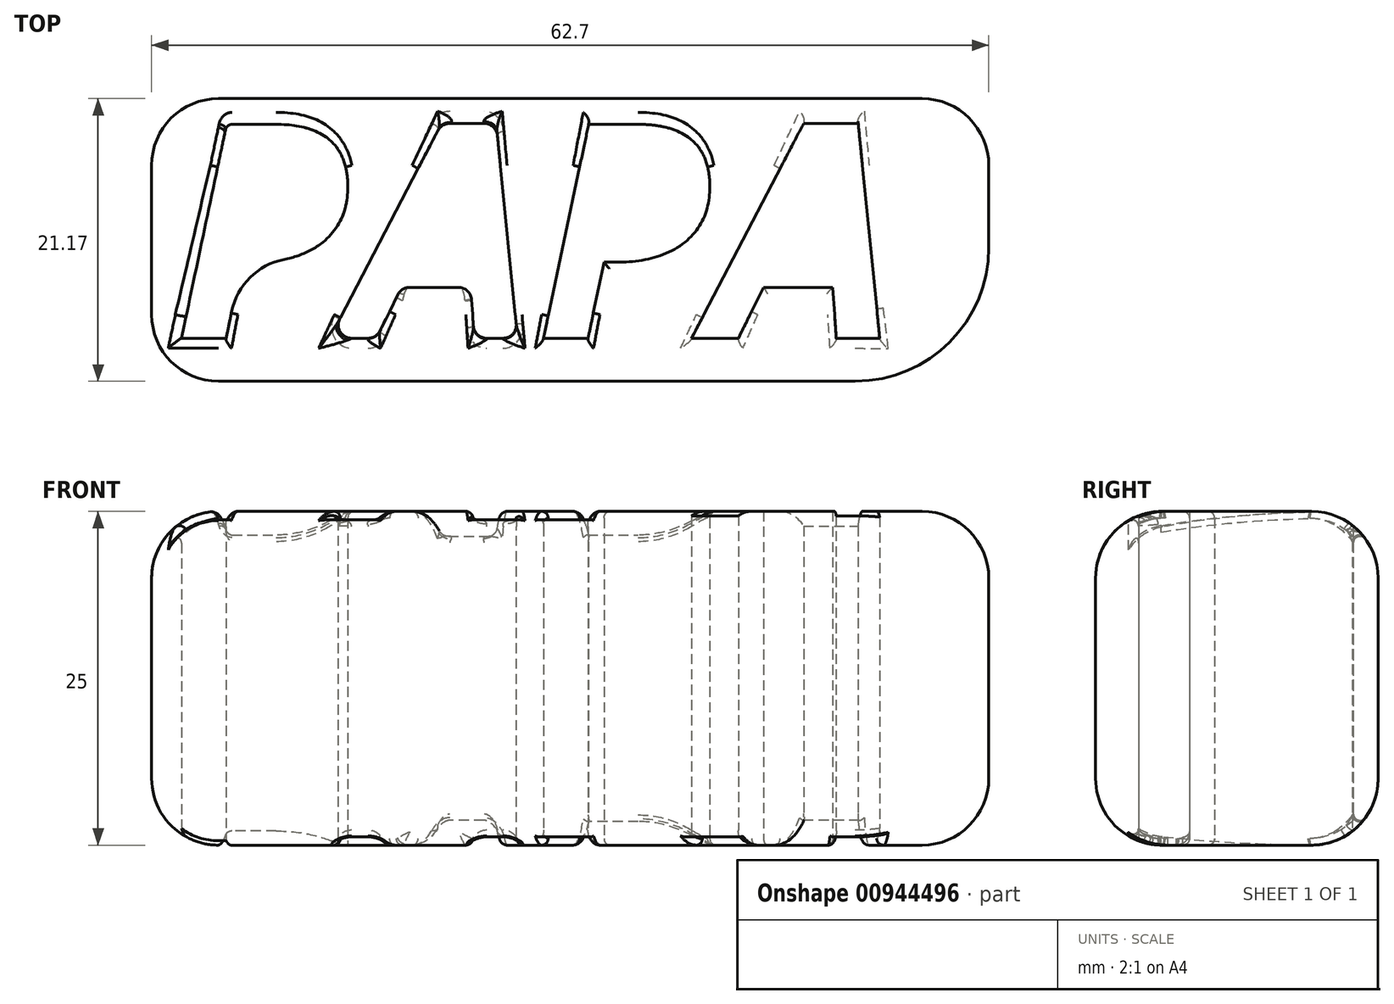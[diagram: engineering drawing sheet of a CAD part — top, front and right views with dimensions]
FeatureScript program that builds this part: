
annotation { "Feature Type Name" : "Feature", "Feature Type Description" : "" }
export const myFeature = defineFeature(function(context is Context, id is Id, definition is map)
    precondition{}
    {
        {
            var Q0;
            Q0=qCreatedBy(makeId("Top.planeOp"),FACE);
            var sketch = newSketch(context, id + "F0", { "sketchPlane" : qUnion([Q0])});
            skText(sketch, "E0", { "text": "PAPA", "fontName": "OpenSans-BoldItalic.ttf"});
            skLineSegment(sketch, "E1.bottom", {"start": v(-61.02, -20.6) * mm, "end": v(-8.32, -20.6) * mm});
            skLineSegment(sketch, "E1.top", {"start": v(-61.02, -41.77) * mm, "end": v(-13.32, -41.77) * mm});
            skLineSegment(sketch, "E1.left", {"start": v(-66.02, -25.6) * mm, "end": v(-66.02, -36.77) * mm});
            skLineSegment(sketch, "E1.right", {"start": v(-3.32, -25.6) * mm, "end": v(-3.32, -31.77) * mm});
            skPoint(sketch, "E2.visualSharp", {"position": v(-3.32, -20.6) * mm});
            skArc(sketch, "E2.filletArc", {"start": v(-3.32, -25.6) * mm, "mid": v(-4.78, -22.07) * mm, "end": v(-8.32, -20.6) * mm});
            skPoint(sketch, "E3.visualSharp", {"position": v(-66.02, -41.77) * mm});
            skArc(sketch, "E3.filletArc", {"start": v(-66.02, -36.77) * mm, "mid": v(-64.56, -40.3) * mm, "end": v(-61.02, -41.77) * mm});
            skPoint(sketch, "E4.visualSharp", {"position": v(-66.02, -20.6) * mm});
            skArc(sketch, "E4.filletArc", {"start": v(-61.02, -20.6) * mm, "mid": v(-64.56, -22.07) * mm, "end": v(-66.02, -25.6) * mm});
            skPoint(sketch, "E5.visualSharp", {"position": v(-3.32, -41.77) * mm});
            skArc(sketch, "E5.filletArc", {"start": v(-13.32, -41.77) * mm, "mid": v(-6.24, -38.84) * mm, "end": v(-3.32, -31.77) * mm});
            const initialGuessF0  = {"E0": [-0.06437, -0.03855, 1, 0, 0.01616]};
            skSetInitialGuess(sketch, initialGuessF0);
            skSolve(sketch);
        }
        {
            var Q0;
            Q0=makeQuery(id+"F0.imprint","IMPRINT",FACE,{"disambiguationData":[TD([[makeQuery(id+"F0.imprint","IMPRINT",EDGE,{"derivedFrom":sQuery(id+"F0.wireOp",EDGE,"E0.sketch_text.stroke-6")}),1.0]])]});
            extrude(context, id + "F1", {"entities" : qUnion([Q0]), "depth" : 25 * mm, "offsetDistance" : 25 * mm});
        }
        {
            var Q0;
            Q0=makeQuery(id+"F1.opExtrude","CAP_EDGE",EDGE,{"disambiguationData":[OSD([sQuery(id+"F0.wireOp",EDGE,"E1.bottom")])],"isStart":false});
            var Q1;
            Q1=makeQuery(id+"F1.opExtrude","CAP_EDGE",EDGE,{"disambiguationData":[OSD([sQuery(id+"F0.wireOp",EDGE,"E1.bottom")])],"isStart":true});
            fillet(context, id + "F2", {"entities" : qUnion([Q0, Q1]), "radius" : 5 * mm, "tangentPropagation" : true, "allowEdgeOverflow" : false});
        }
        {
            var Q0;
            Q0=makeQuery(id+"F2.opFillet","BLEND_EDGE",EDGE,{"blendedFrom":[makeQuery(id+"F1.opExtrude","CAP_EDGE",EDGE,{"disambiguationData":[OSD([sQuery(id+"F0.wireOp",EDGE,"E1.bottom")])],"isStart":false}),makeQuery(id+"F1.opExtrude","SWEPT_FACE",FACE,{"disambiguationData":[OSD([sQuery(id+"F0.wireOp",EDGE,"E0.sketch_text.stroke-12")])]})],"blendedInto":[makeQuery(id+"F1.opExtrude","SWEPT_FACE",FACE,{"disambiguationData":[OSD([sQuery(id+"F0.wireOp",EDGE,"E0.sketch_text.stroke-12")])]})]});
            var Q1;
            Q1=makeQuery(id+"F2.opFillet","BLEND_EDGE",EDGE,{"blendedFrom":[makeQuery(id+"F1.opExtrude","CAP_EDGE",EDGE,{"disambiguationData":[OSD([sQuery(id+"F0.wireOp",EDGE,"E1.bottom")])],"isStart":false}),makeQuery(id+"F1.opExtrude","SWEPT_FACE",FACE,{"disambiguationData":[OSD([sQuery(id+"F0.wireOp",EDGE,"E0.sketch_text.stroke-13")])]})],"blendedInto":[makeQuery(id+"F1.opExtrude","SWEPT_FACE",FACE,{"disambiguationData":[OSD([sQuery(id+"F0.wireOp",EDGE,"E0.sketch_text.stroke-13")])]})]});
            var Q2;
            Q2=makeQuery(id+"F1.opExtrude","CAP_EDGE",EDGE,{"disambiguationData":[OSD([sQuery(id+"F0.wireOp",EDGE,"E0.sketch_text.stroke-14")])],"isStart":false});
            var Q3;
            Q3=makeQuery(id+"F1.opExtrude","CAP_EDGE",EDGE,{"disambiguationData":[OSD([sQuery(id+"F0.wireOp",EDGE,"E0.sketch_text.stroke-6")])],"isStart":false});
            var Q4;
            Q4=makeQuery(id+"F1.opExtrude","CAP_EDGE",EDGE,{"disambiguationData":[OSD([sQuery(id+"F0.wireOp",EDGE,"E0.sketch_text.stroke-7")])],"isStart":false});
            var Q5;
            Q5=makeQuery(id+"F2.opFillet","BLEND_EDGE",EDGE,{"blendedFrom":[makeQuery(id+"F1.opExtrude","CAP_EDGE",EDGE,{"disambiguationData":[OSD([sQuery(id+"F0.wireOp",EDGE,"E1.bottom")])],"isStart":false}),makeQuery(id+"F1.opExtrude","SWEPT_FACE",FACE,{"disambiguationData":[OSD([sQuery(id+"F0.wireOp",EDGE,"E0.sketch_text.stroke-14")])]})],"blendedInto":[makeQuery(id+"F1.opExtrude","SWEPT_FACE",FACE,{"disambiguationData":[OSD([sQuery(id+"F0.wireOp",EDGE,"E0.sketch_text.stroke-14")])]})]});
            var Q6;
            Q6=makeQuery(id+"F1.opExtrude","CAP_EDGE",EDGE,{"disambiguationData":[OSD([sQuery(id+"F0.wireOp",EDGE,"E0.sketch_text.stroke-8")])],"isStart":false});
            var Q7;
            Q7=makeQuery(id+"F1.opExtrude","CAP_EDGE",EDGE,{"disambiguationData":[OSD([sQuery(id+"F0.wireOp",EDGE,"E0.sketch_text.stroke-9")])],"isStart":false});
            var Q8;
            Q8=makeQuery(id+"F2.opFillet","BLEND_EDGE",EDGE,{"blendedFrom":[makeQuery(id+"F1.opExtrude","CAP_EDGE",EDGE,{"disambiguationData":[OSD([sQuery(id+"F0.wireOp",EDGE,"E1.top")])],"isStart":false}),makeQuery(id+"F1.opExtrude","SWEPT_FACE",FACE,{"disambiguationData":[OSD([sQuery(id+"F0.wireOp",EDGE,"E0.sketch_text.stroke-9")])]})],"blendedInto":[makeQuery(id+"F1.opExtrude","SWEPT_FACE",FACE,{"disambiguationData":[OSD([sQuery(id+"F0.wireOp",EDGE,"E0.sketch_text.stroke-9")])]})]});
            var Q9;
            Q9=makeQuery(id+"F2.opFillet","BLEND_EDGE",EDGE,{"disambiguationData":[OD(0.0)],"blendedFrom":[makeQuery(id+"F1.opExtrude","CAP_EDGE",EDGE,{"disambiguationData":[OSD([sQuery(id+"F0.wireOp",EDGE,"E1.top")])],"isStart":false}),makeQuery(id+"F1.opExtrude","SWEPT_FACE",FACE,{"disambiguationData":[OSD([sQuery(id+"F0.wireOp",EDGE,"E0.sketch_text.stroke-10")])]})],"blendedInto":[makeQuery(id+"F1.opExtrude","SWEPT_FACE",FACE,{"disambiguationData":[OSD([sQuery(id+"F0.wireOp",EDGE,"E0.sketch_text.stroke-10")])]})]});
            var Q10;
            Q10=makeQuery(id+"F2.opFillet","BLEND_EDGE",EDGE,{"disambiguationData":[OD(2.0)],"blendedFrom":[makeQuery(id+"F1.opExtrude","CAP_EDGE",EDGE,{"disambiguationData":[OSD([sQuery(id+"F0.wireOp",EDGE,"E1.top")])],"isStart":false}),makeQuery(id+"F1.opExtrude","SWEPT_FACE",FACE,{"disambiguationData":[OSD([sQuery(id+"F0.wireOp",EDGE,"E0.sketch_text.stroke-11")])]})],"blendedInto":[makeQuery(id+"F1.opExtrude","SWEPT_FACE",FACE,{"disambiguationData":[OSD([sQuery(id+"F0.wireOp",EDGE,"E0.sketch_text.stroke-11")])]})]});
            var Q11;
            Q11=makeQuery(id+"F2.opFillet","BLEND_EDGE",EDGE,{"disambiguationData":[OD(1.0)],"blendedFrom":[makeQuery(id+"F1.opExtrude","CAP_EDGE",EDGE,{"disambiguationData":[OSD([sQuery(id+"F0.wireOp",EDGE,"E1.top")])],"isStart":false}),makeQuery(id+"F1.opExtrude","SWEPT_FACE",FACE,{"disambiguationData":[OSD([sQuery(id+"F0.wireOp",EDGE,"E0.sketch_text.stroke-11")])]})],"blendedInto":[makeQuery(id+"F1.opExtrude","SWEPT_FACE",FACE,{"disambiguationData":[OSD([sQuery(id+"F0.wireOp",EDGE,"E0.sketch_text.stroke-11")])]})]});
            var Q12;
            Q12=makeQuery(id+"F2.opFillet","BLEND_EDGE",EDGE,{"blendedFrom":[makeQuery(id+"F1.opExtrude","CAP_EDGE",EDGE,{"disambiguationData":[OSD([sQuery(id+"F0.wireOp",EDGE,"E1.bottom")])],"isStart":false}),makeQuery(id+"F1.opExtrude","SWEPT_FACE",FACE,{"disambiguationData":[OSD([sQuery(id+"F0.wireOp",EDGE,"E0.sketch_text.stroke-11")])]})],"blendedInto":[makeQuery(id+"F1.opExtrude","SWEPT_FACE",FACE,{"disambiguationData":[OSD([sQuery(id+"F0.wireOp",EDGE,"E0.sketch_text.stroke-11")])]})]});
            var Q13;
            Q13=makeQuery(id+"F1.opExtrude","SWEPT_EDGE",EDGE,{"disambiguationData":[OSD([sQuery(id+"F0.wireOp",EDGE,"E0.sketch_text.stroke-11"),sQuery(id+"F0.wireOp",EDGE,"E0.sketch_text.stroke-12")])]});
            var Q14;
            Q14=makeQuery(id+"F2.opFillet","BLEND_EDGE",EDGE,{"disambiguationData":[OD(1.0)],"blendedFrom":[makeQuery(id+"F1.opExtrude","CAP_EDGE",EDGE,{"disambiguationData":[OSD([sQuery(id+"F0.wireOp",EDGE,"E1.top")])],"isStart":false}),makeQuery(id+"F1.opExtrude","SWEPT_FACE",FACE,{"disambiguationData":[OSD([sQuery(id+"F0.wireOp",EDGE,"E0.sketch_text.stroke-10")])]})],"blendedInto":[makeQuery(id+"F1.opExtrude","SWEPT_FACE",FACE,{"disambiguationData":[OSD([sQuery(id+"F0.wireOp",EDGE,"E0.sketch_text.stroke-10")])]})]});
            fillet(context, id + "F3", {"entities" : qUnion([Q0, Q1, Q2, Q3, Q4, Q5, Q6, Q7, Q8, Q9, Q10, Q11, Q12, Q13, Q14]), "radius" : 0.5 * mm, "tangentPropagation" : true, "allowEdgeOverflow" : false});
        }
        {
            var Q0;
            Q0=makeQuery(id+"F2.opFillet","BLEND_EDGE",EDGE,{"blendedFrom":[makeQuery(id+"F1.opExtrude","CAP_EDGE",EDGE,{"disambiguationData":[OSD([sQuery(id+"F0.wireOp",EDGE,"E1.bottom")])],"isStart":false}),makeQuery(id+"F1.opExtrude","SWEPT_FACE",FACE,{"disambiguationData":[OSD([sQuery(id+"F0.wireOp",EDGE,"E0.sketch_text.stroke-20")])]})],"blendedInto":[makeQuery(id+"F1.opExtrude","SWEPT_FACE",FACE,{"disambiguationData":[OSD([sQuery(id+"F0.wireOp",EDGE,"E0.sketch_text.stroke-20")])]})]});
            var Q1;
            Q1=makeQuery(id+"F2.opFillet","BLEND_EDGE",EDGE,{"blendedFrom":[makeQuery(id+"F1.opExtrude","CAP_EDGE",EDGE,{"disambiguationData":[OSD([sQuery(id+"F0.wireOp",EDGE,"E1.bottom")])],"isStart":false}),makeQuery(id+"F1.opExtrude","SWEPT_FACE",FACE,{"disambiguationData":[OSD([sQuery(id+"F0.wireOp",EDGE,"E0.sketch_text.stroke-18")])]})],"blendedInto":[makeQuery(id+"F1.opExtrude","SWEPT_FACE",FACE,{"disambiguationData":[OSD([sQuery(id+"F0.wireOp",EDGE,"E0.sketch_text.stroke-18")])]})]});
            var Q2;
            Q2=makeQuery(id+"F1.opExtrude","CAP_EDGE",EDGE,{"disambiguationData":[OSD([sQuery(id+"F0.wireOp",EDGE,"E0.sketch_text.stroke-18")])],"isStart":false});
            var Q3;
            Q3=makeQuery(id+"F1.opExtrude","CAP_EDGE",EDGE,{"disambiguationData":[OSD([sQuery(id+"F0.wireOp",EDGE,"E0.sketch_text.stroke-20")])],"isStart":false});
            var Q4;
            Q4=makeQuery(id+"F2.opFillet","BLEND_EDGE",EDGE,{"blendedFrom":[makeQuery(id+"F1.opExtrude","CAP_EDGE",EDGE,{"disambiguationData":[OSD([sQuery(id+"F0.wireOp",EDGE,"E1.top")])],"isStart":false}),makeQuery(id+"F1.opExtrude","SWEPT_FACE",FACE,{"disambiguationData":[OSD([sQuery(id+"F0.wireOp",EDGE,"E0.sketch_text.stroke-20")])]})],"blendedInto":[makeQuery(id+"F1.opExtrude","SWEPT_FACE",FACE,{"disambiguationData":[OSD([sQuery(id+"F0.wireOp",EDGE,"E0.sketch_text.stroke-20")])]})]});
            var Q5;
            Q5=makeQuery(id+"F2.opFillet","BLEND_EDGE",EDGE,{"blendedFrom":[makeQuery(id+"F1.opExtrude","CAP_EDGE",EDGE,{"disambiguationData":[OSD([sQuery(id+"F0.wireOp",EDGE,"E1.top")])],"isStart":false}),makeQuery(id+"F1.opExtrude","SWEPT_FACE",FACE,{"disambiguationData":[OSD([sQuery(id+"F0.wireOp",EDGE,"E0.sketch_text.stroke-21")])]})],"blendedInto":[makeQuery(id+"F1.opExtrude","SWEPT_FACE",FACE,{"disambiguationData":[OSD([sQuery(id+"F0.wireOp",EDGE,"E0.sketch_text.stroke-21")])]})]});
            var Q6;
            Q6=makeQuery(id+"F2.opFillet","BLEND_EDGE",EDGE,{"blendedFrom":[makeQuery(id+"F1.opExtrude","CAP_EDGE",EDGE,{"disambiguationData":[OSD([sQuery(id+"F0.wireOp",EDGE,"E1.top")])],"isStart":false}),makeQuery(id+"F1.opExtrude","SWEPT_FACE",FACE,{"disambiguationData":[OSD([sQuery(id+"F0.wireOp",EDGE,"E0.sketch_text.stroke-22")])]})],"blendedInto":[makeQuery(id+"F1.opExtrude","SWEPT_FACE",FACE,{"disambiguationData":[OSD([sQuery(id+"F0.wireOp",EDGE,"E0.sketch_text.stroke-22")])]})]});
            var Q7;
            Q7=makeQuery(id+"F1.opExtrude","CAP_EDGE",EDGE,{"disambiguationData":[OSD([sQuery(id+"F0.wireOp",EDGE,"E0.sketch_text.stroke-22")])],"isStart":false});
            var Q8;
            Q8=makeQuery(id+"F1.opExtrude","CAP_EDGE",EDGE,{"disambiguationData":[OSD([sQuery(id+"F0.wireOp",EDGE,"E0.sketch_text.stroke-15")])],"isStart":false});
            var Q9;
            Q9=makeQuery(id+"F1.opExtrude","CAP_EDGE",EDGE,{"disambiguationData":[OSD([sQuery(id+"F0.wireOp",EDGE,"E0.sketch_text.stroke-16")])],"isStart":false});
            var Q10;
            Q10=makeQuery(id+"F2.opFillet","BLEND_EDGE",EDGE,{"blendedFrom":[makeQuery(id+"F1.opExtrude","CAP_EDGE",EDGE,{"disambiguationData":[OSD([sQuery(id+"F0.wireOp",EDGE,"E1.top")])],"isStart":false}),makeQuery(id+"F1.opExtrude","SWEPT_FACE",FACE,{"disambiguationData":[OSD([sQuery(id+"F0.wireOp",EDGE,"E0.sketch_text.stroke-16")])]})],"blendedInto":[makeQuery(id+"F1.opExtrude","SWEPT_FACE",FACE,{"disambiguationData":[OSD([sQuery(id+"F0.wireOp",EDGE,"E0.sketch_text.stroke-16")])]})]});
            var Q11;
            Q11=makeQuery(id+"F2.opFillet","BLEND_EDGE",EDGE,{"blendedFrom":[makeQuery(id+"F1.opExtrude","CAP_EDGE",EDGE,{"disambiguationData":[OSD([sQuery(id+"F0.wireOp",EDGE,"E1.top")])],"isStart":false}),makeQuery(id+"F1.opExtrude","SWEPT_FACE",FACE,{"disambiguationData":[OSD([sQuery(id+"F0.wireOp",EDGE,"E0.sketch_text.stroke-17")])]})],"blendedInto":[makeQuery(id+"F1.opExtrude","SWEPT_FACE",FACE,{"disambiguationData":[OSD([sQuery(id+"F0.wireOp",EDGE,"E0.sketch_text.stroke-17")])]})]});
            var Q12;
            Q12=makeQuery(id+"F2.opFillet","BLEND_EDGE",EDGE,{"blendedFrom":[makeQuery(id+"F1.opExtrude","CAP_EDGE",EDGE,{"disambiguationData":[OSD([sQuery(id+"F0.wireOp",EDGE,"E1.top")])],"isStart":false}),makeQuery(id+"F1.opExtrude","SWEPT_FACE",FACE,{"disambiguationData":[OSD([sQuery(id+"F0.wireOp",EDGE,"E0.sketch_text.stroke-18")])]})],"blendedInto":[makeQuery(id+"F1.opExtrude","SWEPT_FACE",FACE,{"disambiguationData":[OSD([sQuery(id+"F0.wireOp",EDGE,"E0.sketch_text.stroke-18")])]})]});
            var Q13;
            Q13=makeQuery(id+"F2.opFillet","BLEND_EDGE",EDGE,{"blendedFrom":[makeQuery(id+"F1.opExtrude","CAP_EDGE",EDGE,{"disambiguationData":[OSD([sQuery(id+"F0.wireOp",EDGE,"E1.bottom")])],"isStart":false}),makeQuery(id+"F1.opExtrude","SWEPT_FACE",FACE,{"disambiguationData":[OSD([sQuery(id+"F0.wireOp",EDGE,"E0.sketch_text.stroke-19")])]})],"blendedInto":[makeQuery(id+"F1.opExtrude","SWEPT_FACE",FACE,{"disambiguationData":[OSD([sQuery(id+"F0.wireOp",EDGE,"E0.sketch_text.stroke-19")])]})]});
            fillet(context, id + "F4", {"entities" : qUnion([Q0, Q1, Q2, Q3, Q4, Q5, Q6, Q7, Q8, Q9, Q10, Q11, Q12, Q13]), "radius" : 0.5 * mm, "tangentPropagation" : true, "allowEdgeOverflow" : false});
        }
        {
            var Q0;
            Q0=makeQuery(id+"F1.opExtrude","SWEPT_EDGE",EDGE,{"disambiguationData":[OSD([sQuery(id+"F0.wireOp",EDGE,"E0.sketch_text.stroke-8"),sQuery(id+"F0.wireOp",EDGE,"E0.sketch_text.stroke-9")])]});
            fillet(context, id + "F5", {"entities" : qUnion([Q0]), "radius" : 5 * mm, "tangentPropagation" : true, "allowEdgeOverflow" : false});
        }
        {
            var Q0;
            Q0=makeQuery(id+"F1.opExtrude","SWEPT_EDGE",EDGE,{"disambiguationData":[OSD([sQuery(id+"F0.wireOp",EDGE,"E0.sketch_text.stroke-15"),sQuery(id+"F0.wireOp",EDGE,"E0.sketch_text.stroke-16")])]});
            var Q1;
            Q1=makeQuery(id+"F1.opExtrude","SWEPT_FACE",FACE,{"disambiguationData":[OSD([sQuery(id+"F0.wireOp",EDGE,"E0.sketch_text.stroke-15")])]});
            var Q2;
            Q2=makeQuery(id+"F1.opExtrude","SWEPT_EDGE",EDGE,{"disambiguationData":[OSD([sQuery(id+"F0.wireOp",EDGE,"E0.sketch_text.stroke-20"),sQuery(id+"F0.wireOp",EDGE,"E0.sketch_text.stroke-21")])]});
            var Q3;
            Q3=makeQuery(id+"F1.opExtrude","SWEPT_EDGE",EDGE,{"disambiguationData":[OSD([sQuery(id+"F0.wireOp",EDGE,"E0.sketch_text.stroke-21"),sQuery(id+"F0.wireOp",EDGE,"E0.sketch_text.stroke-22")])]});
            var Q4;
            Q4=makeQuery(id+"F1.opExtrude","SWEPT_EDGE",EDGE,{"disambiguationData":[OSD([sQuery(id+"F0.wireOp",EDGE,"E0.sketch_text.stroke-16"),sQuery(id+"F0.wireOp",EDGE,"E0.sketch_text.stroke-17")])]});
            var Q5;
            Q5=makeQuery(id+"F1.opExtrude","SWEPT_EDGE",EDGE,{"disambiguationData":[OSD([sQuery(id+"F0.wireOp",EDGE,"E0.sketch_text.stroke-17"),sQuery(id+"F0.wireOp",EDGE,"E0.sketch_text.stroke-18")])]});
            var Q6;
            Q6=makeQuery(id+"F1.opExtrude","SWEPT_EDGE",EDGE,{"disambiguationData":[OSD([sQuery(id+"F0.wireOp",EDGE,"E0.sketch_text.stroke-19"),sQuery(id+"F0.wireOp",EDGE,"E0.sketch_text.stroke-20")])]});
            var Q7;
            Q7=makeQuery(id+"F1.opExtrude","SWEPT_EDGE",EDGE,{"disambiguationData":[OSD([sQuery(id+"F0.wireOp",EDGE,"E0.sketch_text.stroke-18"),sQuery(id+"F0.wireOp",EDGE,"E0.sketch_text.stroke-19")])]});
            fillet(context, id + "F6", {"entities" : qUnion([Q0, Q1, Q2, Q3, Q4, Q5, Q6, Q7]), "radius" : 1 * mm, "tangentPropagation" : true, "allowEdgeOverflow" : false});
        }
        {
            var Q0;
            Q0=makeQuery(id+"F2.opFillet","BLEND_EDGE",EDGE,{"blendedFrom":[makeQuery(id+"F1.opExtrude","CAP_EDGE",EDGE,{"disambiguationData":[OSD([sQuery(id+"F0.wireOp",EDGE,"E1.bottom")])],"isStart":false}),makeQuery(id+"F1.opExtrude","SWEPT_FACE",FACE,{"disambiguationData":[OSD([sQuery(id+"F0.wireOp",EDGE,"E0.sketch_text.stroke-41")])]})],"blendedInto":[makeQuery(id+"F1.opExtrude","SWEPT_FACE",FACE,{"disambiguationData":[OSD([sQuery(id+"F0.wireOp",EDGE,"E0.sketch_text.stroke-41")])]})]});
            var Q1;
            Q1=makeQuery(id+"F2.opFillet","BLEND_EDGE",EDGE,{"blendedFrom":[makeQuery(id+"F1.opExtrude","CAP_EDGE",EDGE,{"disambiguationData":[OSD([sQuery(id+"F0.wireOp",EDGE,"E1.bottom")])],"isStart":false}),makeQuery(id+"F1.opExtrude","SWEPT_FACE",FACE,{"disambiguationData":[OSD([sQuery(id+"F0.wireOp",EDGE,"E0.sketch_text.stroke-42")])]})],"blendedInto":[makeQuery(id+"F1.opExtrude","SWEPT_FACE",FACE,{"disambiguationData":[OSD([sQuery(id+"F0.wireOp",EDGE,"E0.sketch_text.stroke-42")])]})]});
            var Q2;
            Q2=makeQuery(id+"F2.opFillet","BLEND_EDGE",EDGE,{"blendedFrom":[makeQuery(id+"F1.opExtrude","CAP_EDGE",EDGE,{"disambiguationData":[OSD([sQuery(id+"F0.wireOp",EDGE,"E1.bottom")])],"isStart":false}),makeQuery(id+"F1.opExtrude","SWEPT_FACE",FACE,{"disambiguationData":[OSD([sQuery(id+"F0.wireOp",EDGE,"E0.sketch_text.stroke-43")])]})],"blendedInto":[makeQuery(id+"F1.opExtrude","SWEPT_FACE",FACE,{"disambiguationData":[OSD([sQuery(id+"F0.wireOp",EDGE,"E0.sketch_text.stroke-43")])]})]});
            var Q3;
            Q3=makeQuery(id+"F1.opExtrude","CAP_EDGE",EDGE,{"disambiguationData":[OSD([sQuery(id+"F0.wireOp",EDGE,"E0.sketch_text.stroke-43")])],"isStart":false});
            var Q4;
            Q4=makeQuery(id+"F1.opExtrude","CAP_EDGE",EDGE,{"disambiguationData":[OSD([sQuery(id+"F0.wireOp",EDGE,"E0.sketch_text.stroke-35")])],"isStart":false});
            var Q5;
            Q5=makeQuery(id+"F1.opExtrude","CAP_EDGE",EDGE,{"disambiguationData":[OSD([sQuery(id+"F0.wireOp",EDGE,"E0.sketch_text.stroke-36")])],"isStart":false});
            var Q6;
            Q6=makeQuery(id+"F1.opExtrude","CAP_EDGE",EDGE,{"disambiguationData":[OSD([sQuery(id+"F0.wireOp",EDGE,"E0.sketch_text.stroke-38")])],"isStart":false});
            var Q7;
            Q7=makeQuery(id+"F2.opFillet","BLEND_EDGE",EDGE,{"blendedFrom":[makeQuery(id+"F1.opExtrude","CAP_EDGE",EDGE,{"disambiguationData":[OSD([sQuery(id+"F0.wireOp",EDGE,"E1.top")])],"isStart":false}),makeQuery(id+"F1.opExtrude","SWEPT_FACE",FACE,{"disambiguationData":[OSD([sQuery(id+"F0.wireOp",EDGE,"E0.sketch_text.stroke-38")])]})],"blendedInto":[makeQuery(id+"F1.opExtrude","SWEPT_FACE",FACE,{"disambiguationData":[OSD([sQuery(id+"F0.wireOp",EDGE,"E0.sketch_text.stroke-38")])]})]});
            var Q8;
            Q8=makeQuery(id+"F2.opFillet","BLEND_EDGE",EDGE,{"blendedFrom":[makeQuery(id+"F1.opExtrude","CAP_EDGE",EDGE,{"disambiguationData":[OSD([sQuery(id+"F0.wireOp",EDGE,"E1.top")])],"isStart":false}),makeQuery(id+"F1.opExtrude","SWEPT_FACE",FACE,{"disambiguationData":[OSD([sQuery(id+"F0.wireOp",EDGE,"E0.sketch_text.stroke-39")])]})],"blendedInto":[makeQuery(id+"F1.opExtrude","SWEPT_FACE",FACE,{"disambiguationData":[OSD([sQuery(id+"F0.wireOp",EDGE,"E0.sketch_text.stroke-39")])]})]});
            var Q9;
            Q9=makeQuery(id+"F2.opFillet","BLEND_EDGE",EDGE,{"blendedFrom":[makeQuery(id+"F1.opExtrude","CAP_EDGE",EDGE,{"disambiguationData":[OSD([sQuery(id+"F0.wireOp",EDGE,"E1.top")])],"isStart":false}),makeQuery(id+"F1.opExtrude","SWEPT_FACE",FACE,{"disambiguationData":[OSD([sQuery(id+"F0.wireOp",EDGE,"E0.sketch_text.stroke-40")])]})],"blendedInto":[makeQuery(id+"F1.opExtrude","SWEPT_FACE",FACE,{"disambiguationData":[OSD([sQuery(id+"F0.wireOp",EDGE,"E0.sketch_text.stroke-40")])]})]});
            var Q10;
            Q10=makeQuery(id+"F1.opExtrude","CAP_EDGE",EDGE,{"disambiguationData":[OSD([sQuery(id+"F0.wireOp",EDGE,"E0.sketch_text.stroke-40")])],"isStart":false});
            var Q11;
            Q11=makeQuery(id+"F2.opFillet","BLEND_EDGE",EDGE,{"blendedFrom":[makeQuery(id+"F1.opExtrude","CAP_EDGE",EDGE,{"disambiguationData":[OSD([sQuery(id+"F0.wireOp",EDGE,"E1.bottom")])],"isStart":false}),makeQuery(id+"F1.opExtrude","SWEPT_FACE",FACE,{"disambiguationData":[OSD([sQuery(id+"F0.wireOp",EDGE,"E0.sketch_text.stroke-40")])]})],"blendedInto":[makeQuery(id+"F1.opExtrude","SWEPT_FACE",FACE,{"disambiguationData":[OSD([sQuery(id+"F0.wireOp",EDGE,"E0.sketch_text.stroke-40")])]})]});
            var Q12;
            Q12=makeQuery(id+"F1.opExtrude","CAP_EDGE",EDGE,{"disambiguationData":[OSD([sQuery(id+"F0.wireOp",EDGE,"E0.sketch_text.stroke-37")])],"isStart":false});
            fillet(context, id + "F7", {"entities" : qUnion([Q0, Q1, Q2, Q3, Q4, Q5, Q6, Q7, Q8, Q9, Q10, Q11, Q12]), "radius" : 0.5 * mm, "tangentPropagation" : true, "allowEdgeOverflow" : false});
        }
        {
            var Q0;
            Q0=makeQuery(id+"F2.opFillet","BLEND_EDGE",EDGE,{"blendedFrom":[makeQuery(id+"F1.opExtrude","CAP_EDGE",EDGE,{"disambiguationData":[OSD([sQuery(id+"F0.wireOp",EDGE,"E1.bottom")])],"isStart":true}),makeQuery(id+"F1.opExtrude","SWEPT_FACE",FACE,{"disambiguationData":[OSD([sQuery(id+"F0.wireOp",EDGE,"E0.sketch_text.stroke-47")])]})],"blendedInto":[makeQuery(id+"F1.opExtrude","SWEPT_FACE",FACE,{"disambiguationData":[OSD([sQuery(id+"F0.wireOp",EDGE,"E0.sketch_text.stroke-47")])]})]});
            var Q1;
            Q1=makeQuery(id+"F2.opFillet","BLEND_EDGE",EDGE,{"blendedFrom":[makeQuery(id+"F1.opExtrude","CAP_EDGE",EDGE,{"disambiguationData":[OSD([sQuery(id+"F0.wireOp",EDGE,"E1.bottom")])],"isStart":true}),makeQuery(id+"F1.opExtrude","SWEPT_FACE",FACE,{"disambiguationData":[OSD([sQuery(id+"F0.wireOp",EDGE,"E0.sketch_text.stroke-48")])]})],"blendedInto":[makeQuery(id+"F1.opExtrude","SWEPT_FACE",FACE,{"disambiguationData":[OSD([sQuery(id+"F0.wireOp",EDGE,"E0.sketch_text.stroke-48")])]})]});
            var Q2;
            Q2=makeQuery(id+"F1.opExtrude","CAP_EDGE",EDGE,{"disambiguationData":[OSD([sQuery(id+"F0.wireOp",EDGE,"E0.sketch_text.stroke-49")])],"isStart":true});
            var Q3;
            Q3=makeQuery(id+"F2.opFillet","BLEND_EDGE",EDGE,{"blendedFrom":[makeQuery(id+"F1.opExtrude","CAP_EDGE",EDGE,{"disambiguationData":[OSD([sQuery(id+"F0.wireOp",EDGE,"E5.filletArc")])],"isStart":true}),makeQuery(id+"F1.opExtrude","SWEPT_FACE",FACE,{"disambiguationData":[OSD([sQuery(id+"F0.wireOp",EDGE,"E0.sketch_text.stroke-49")])]})],"blendedInto":[makeQuery(id+"F1.opExtrude","SWEPT_FACE",FACE,{"disambiguationData":[OSD([sQuery(id+"F0.wireOp",EDGE,"E0.sketch_text.stroke-49")])]})]});
            var Q4;
            Q4=makeQuery(id+"F2.opFillet","BLEND_EDGE",EDGE,{"blendedFrom":[makeQuery(id+"F1.opExtrude","CAP_EDGE",EDGE,{"disambiguationData":[OSD([sQuery(id+"F0.wireOp",EDGE,"E5.filletArc")])],"isStart":true}),makeQuery(id+"F1.opExtrude","SWEPT_FACE",FACE,{"disambiguationData":[OSD([sQuery(id+"F0.wireOp",EDGE,"E0.sketch_text.stroke-50")])]})],"blendedInto":[makeQuery(id+"F1.opExtrude","SWEPT_FACE",FACE,{"disambiguationData":[OSD([sQuery(id+"F0.wireOp",EDGE,"E0.sketch_text.stroke-50")])]})]});
            var Q5;
            Q5=makeQuery(id+"F2.opFillet","BLEND_EDGE",EDGE,{"blendedFrom":[makeQuery(id+"F1.opExtrude","CAP_EDGE",EDGE,{"disambiguationData":[OSD([sQuery(id+"F0.wireOp",EDGE,"E1.top")])],"isStart":true}),makeQuery(id+"F1.opExtrude","SWEPT_FACE",FACE,{"disambiguationData":[OSD([sQuery(id+"F0.wireOp",EDGE,"E0.sketch_text.stroke-50")])]})],"blendedInto":[makeQuery(id+"F1.opExtrude","SWEPT_FACE",FACE,{"disambiguationData":[OSD([sQuery(id+"F0.wireOp",EDGE,"E0.sketch_text.stroke-50")])]})]});
            var Q6;
            Q6=makeQuery(id+"F2.opFillet","BLEND_EDGE",EDGE,{"blendedFrom":[makeQuery(id+"F1.opExtrude","CAP_EDGE",EDGE,{"disambiguationData":[OSD([sQuery(id+"F0.wireOp",EDGE,"E1.top")])],"isStart":true}),makeQuery(id+"F1.opExtrude","SWEPT_FACE",FACE,{"disambiguationData":[OSD([sQuery(id+"F0.wireOp",EDGE,"E0.sketch_text.stroke-51")])]})],"blendedInto":[makeQuery(id+"F1.opExtrude","SWEPT_FACE",FACE,{"disambiguationData":[OSD([sQuery(id+"F0.wireOp",EDGE,"E0.sketch_text.stroke-51")])]})]});
            var Q7;
            Q7=makeQuery(id+"F1.opExtrude","CAP_EDGE",EDGE,{"disambiguationData":[OSD([sQuery(id+"F0.wireOp",EDGE,"E0.sketch_text.stroke-51")])],"isStart":true});
            var Q8;
            Q8=makeQuery(id+"F1.opExtrude","CAP_EDGE",EDGE,{"disambiguationData":[OSD([sQuery(id+"F0.wireOp",EDGE,"E0.sketch_text.stroke-44")])],"isStart":true});
            var Q9;
            Q9=makeQuery(id+"F1.opExtrude","CAP_EDGE",EDGE,{"disambiguationData":[OSD([sQuery(id+"F0.wireOp",EDGE,"E0.sketch_text.stroke-45")])],"isStart":true});
            var Q10;
            Q10=makeQuery(id+"F2.opFillet","BLEND_EDGE",EDGE,{"blendedFrom":[makeQuery(id+"F1.opExtrude","CAP_EDGE",EDGE,{"disambiguationData":[OSD([sQuery(id+"F0.wireOp",EDGE,"E1.top")])],"isStart":true}),makeQuery(id+"F1.opExtrude","SWEPT_FACE",FACE,{"disambiguationData":[OSD([sQuery(id+"F0.wireOp",EDGE,"E0.sketch_text.stroke-45")])]})],"blendedInto":[makeQuery(id+"F1.opExtrude","SWEPT_FACE",FACE,{"disambiguationData":[OSD([sQuery(id+"F0.wireOp",EDGE,"E0.sketch_text.stroke-45")])]})]});
            var Q11;
            Q11=makeQuery(id+"F2.opFillet","BLEND_EDGE",EDGE,{"blendedFrom":[makeQuery(id+"F1.opExtrude","CAP_EDGE",EDGE,{"disambiguationData":[OSD([sQuery(id+"F0.wireOp",EDGE,"E1.top")])],"isStart":true}),makeQuery(id+"F1.opExtrude","SWEPT_FACE",FACE,{"disambiguationData":[OSD([sQuery(id+"F0.wireOp",EDGE,"E0.sketch_text.stroke-46")])]})],"blendedInto":[makeQuery(id+"F1.opExtrude","SWEPT_FACE",FACE,{"disambiguationData":[OSD([sQuery(id+"F0.wireOp",EDGE,"E0.sketch_text.stroke-46")])]})]});
            var Q12;
            Q12=makeQuery(id+"F1.opExtrude","CAP_EDGE",EDGE,{"disambiguationData":[OSD([sQuery(id+"F0.wireOp",EDGE,"E0.sketch_text.stroke-47")])],"isStart":true});
            var Q13;
            Q13=makeQuery(id+"F2.opFillet","BLEND_EDGE",EDGE,{"blendedFrom":[makeQuery(id+"F1.opExtrude","CAP_EDGE",EDGE,{"disambiguationData":[OSD([sQuery(id+"F0.wireOp",EDGE,"E1.top")])],"isStart":true}),makeQuery(id+"F1.opExtrude","SWEPT_FACE",FACE,{"disambiguationData":[OSD([sQuery(id+"F0.wireOp",EDGE,"E0.sketch_text.stroke-47")])]})],"blendedInto":[makeQuery(id+"F1.opExtrude","SWEPT_FACE",FACE,{"disambiguationData":[OSD([sQuery(id+"F0.wireOp",EDGE,"E0.sketch_text.stroke-47")])]})]});
            var Q14;
            Q14=makeQuery(id+"F2.opFillet","BLEND_EDGE",EDGE,{"blendedFrom":[makeQuery(id+"F1.opExtrude","CAP_EDGE",EDGE,{"disambiguationData":[OSD([sQuery(id+"F0.wireOp",EDGE,"E1.bottom")])],"isStart":true}),makeQuery(id+"F1.opExtrude","SWEPT_FACE",FACE,{"disambiguationData":[OSD([sQuery(id+"F0.wireOp",EDGE,"E0.sketch_text.stroke-49")])]})],"blendedInto":[makeQuery(id+"F1.opExtrude","SWEPT_FACE",FACE,{"disambiguationData":[OSD([sQuery(id+"F0.wireOp",EDGE,"E0.sketch_text.stroke-49")])]})]});
            var Q15;
            Q15=makeQuery(id+"F1.opExtrude","CAP_EDGE",EDGE,{"disambiguationData":[OSD([sQuery(id+"F0.wireOp",EDGE,"E0.sketch_text.stroke-40")])],"isStart":true});
            var Q16;
            Q16=makeQuery(id+"F2.opFillet","BLEND_EDGE",EDGE,{"blendedFrom":[makeQuery(id+"F1.opExtrude","CAP_EDGE",EDGE,{"disambiguationData":[OSD([sQuery(id+"F0.wireOp",EDGE,"E1.bottom")])],"isStart":true}),makeQuery(id+"F1.opExtrude","SWEPT_FACE",FACE,{"disambiguationData":[OSD([sQuery(id+"F0.wireOp",EDGE,"E0.sketch_text.stroke-40")])]})],"blendedInto":[makeQuery(id+"F1.opExtrude","SWEPT_FACE",FACE,{"disambiguationData":[OSD([sQuery(id+"F0.wireOp",EDGE,"E0.sketch_text.stroke-40")])]})]});
            var Q17;
            Q17=makeQuery(id+"F2.opFillet","BLEND_EDGE",EDGE,{"blendedFrom":[makeQuery(id+"F1.opExtrude","CAP_EDGE",EDGE,{"disambiguationData":[OSD([sQuery(id+"F0.wireOp",EDGE,"E1.bottom")])],"isStart":true}),makeQuery(id+"F1.opExtrude","SWEPT_FACE",FACE,{"disambiguationData":[OSD([sQuery(id+"F0.wireOp",EDGE,"E0.sketch_text.stroke-41")])]})],"blendedInto":[makeQuery(id+"F1.opExtrude","SWEPT_FACE",FACE,{"disambiguationData":[OSD([sQuery(id+"F0.wireOp",EDGE,"E0.sketch_text.stroke-41")])]})]});
            var Q18;
            Q18=makeQuery(id+"F1.opExtrude","CAP_EDGE",EDGE,{"disambiguationData":[OSD([sQuery(id+"F0.wireOp",EDGE,"E0.sketch_text.stroke-37")])],"isStart":true});
            var Q19;
            Q19=makeQuery(id+"F1.opExtrude","CAP_EDGE",EDGE,{"disambiguationData":[OSD([sQuery(id+"F0.wireOp",EDGE,"E0.sketch_text.stroke-38")])],"isStart":true});
            var Q20;
            Q20=makeQuery(id+"F2.opFillet","BLEND_EDGE",EDGE,{"blendedFrom":[makeQuery(id+"F1.opExtrude","CAP_EDGE",EDGE,{"disambiguationData":[OSD([sQuery(id+"F0.wireOp",EDGE,"E1.top")])],"isStart":true}),makeQuery(id+"F1.opExtrude","SWEPT_FACE",FACE,{"disambiguationData":[OSD([sQuery(id+"F0.wireOp",EDGE,"E0.sketch_text.stroke-38")])]})],"blendedInto":[makeQuery(id+"F1.opExtrude","SWEPT_FACE",FACE,{"disambiguationData":[OSD([sQuery(id+"F0.wireOp",EDGE,"E0.sketch_text.stroke-38")])]})]});
            var Q21;
            Q21=makeQuery(id+"F2.opFillet","BLEND_EDGE",EDGE,{"blendedFrom":[makeQuery(id+"F1.opExtrude","CAP_EDGE",EDGE,{"disambiguationData":[OSD([sQuery(id+"F0.wireOp",EDGE,"E1.top")])],"isStart":true}),makeQuery(id+"F1.opExtrude","SWEPT_FACE",FACE,{"disambiguationData":[OSD([sQuery(id+"F0.wireOp",EDGE,"E0.sketch_text.stroke-40")])]})],"blendedInto":[makeQuery(id+"F1.opExtrude","SWEPT_FACE",FACE,{"disambiguationData":[OSD([sQuery(id+"F0.wireOp",EDGE,"E0.sketch_text.stroke-40")])]})]});
            var Q22;
            Q22=makeQuery(id+"F1.opExtrude","CAP_EDGE",EDGE,{"disambiguationData":[OSD([sQuery(id+"F0.wireOp",EDGE,"E0.sketch_text.stroke-18")])],"isStart":true});
            var Q23;
            Q23=makeQuery(id+"F2.opFillet","BLEND_EDGE",EDGE,{"blendedFrom":[makeQuery(id+"F1.opExtrude","CAP_EDGE",EDGE,{"disambiguationData":[OSD([sQuery(id+"F0.wireOp",EDGE,"E1.bottom")])],"isStart":true}),makeQuery(id+"F1.opExtrude","SWEPT_FACE",FACE,{"disambiguationData":[OSD([sQuery(id+"F0.wireOp",EDGE,"E0.sketch_text.stroke-18")])]})],"blendedInto":[makeQuery(id+"F1.opExtrude","SWEPT_FACE",FACE,{"disambiguationData":[OSD([sQuery(id+"F0.wireOp",EDGE,"E0.sketch_text.stroke-18")])]})]});
            var Q24;
            Q24=makeQuery(id+"F2.opFillet","BLEND_EDGE",EDGE,{"blendedFrom":[makeQuery(id+"F1.opExtrude","CAP_EDGE",EDGE,{"disambiguationData":[OSD([sQuery(id+"F0.wireOp",EDGE,"E1.bottom")])],"isStart":true}),makeQuery(id+"F1.opExtrude","SWEPT_FACE",FACE,{"disambiguationData":[OSD([sQuery(id+"F0.wireOp",EDGE,"E0.sketch_text.stroke-19")])]})],"blendedInto":[makeQuery(id+"F1.opExtrude","SWEPT_FACE",FACE,{"disambiguationData":[OSD([sQuery(id+"F0.wireOp",EDGE,"E0.sketch_text.stroke-19")])]})]});
            var Q25;
            Q25=makeQuery(id+"F2.opFillet","BLEND_EDGE",EDGE,{"blendedFrom":[makeQuery(id+"F1.opExtrude","CAP_EDGE",EDGE,{"disambiguationData":[OSD([sQuery(id+"F0.wireOp",EDGE,"E1.bottom")])],"isStart":true}),makeQuery(id+"F1.opExtrude","SWEPT_FACE",FACE,{"disambiguationData":[OSD([sQuery(id+"F0.wireOp",EDGE,"E0.sketch_text.stroke-42")])]})],"blendedInto":[makeQuery(id+"F1.opExtrude","SWEPT_FACE",FACE,{"disambiguationData":[OSD([sQuery(id+"F0.wireOp",EDGE,"E0.sketch_text.stroke-42")])]})]});
            var Q26;
            Q26=makeQuery(id+"F2.opFillet","BLEND_EDGE",EDGE,{"blendedFrom":[makeQuery(id+"F1.opExtrude","CAP_EDGE",EDGE,{"disambiguationData":[OSD([sQuery(id+"F0.wireOp",EDGE,"E1.bottom")])],"isStart":true}),makeQuery(id+"F1.opExtrude","SWEPT_FACE",FACE,{"disambiguationData":[OSD([sQuery(id+"F0.wireOp",EDGE,"E0.sketch_text.stroke-43")])]})],"blendedInto":[makeQuery(id+"F1.opExtrude","SWEPT_FACE",FACE,{"disambiguationData":[OSD([sQuery(id+"F0.wireOp",EDGE,"E0.sketch_text.stroke-43")])]})]});
            var Q27;
            Q27=makeQuery(id+"F1.opExtrude","CAP_EDGE",EDGE,{"disambiguationData":[OSD([sQuery(id+"F0.wireOp",EDGE,"E0.sketch_text.stroke-35")])],"isStart":true});
            var Q28;
            Q28=makeQuery(id+"F1.opExtrude","CAP_EDGE",EDGE,{"disambiguationData":[OSD([sQuery(id+"F0.wireOp",EDGE,"E0.sketch_text.stroke-43")])],"isStart":true});
            var Q29;
            Q29=makeQuery(id+"F1.opExtrude","CAP_EDGE",EDGE,{"disambiguationData":[OSD([sQuery(id+"F0.wireOp",EDGE,"E0.sketch_text.stroke-36")])],"isStart":true});
            var Q30;
            Q30=makeQuery(id+"F2.opFillet","BLEND_EDGE",EDGE,{"blendedFrom":[makeQuery(id+"F1.opExtrude","CAP_EDGE",EDGE,{"disambiguationData":[OSD([sQuery(id+"F0.wireOp",EDGE,"E1.top")])],"isStart":true}),makeQuery(id+"F1.opExtrude","SWEPT_FACE",FACE,{"disambiguationData":[OSD([sQuery(id+"F0.wireOp",EDGE,"E0.sketch_text.stroke-39")])]})],"blendedInto":[makeQuery(id+"F1.opExtrude","SWEPT_FACE",FACE,{"disambiguationData":[OSD([sQuery(id+"F0.wireOp",EDGE,"E0.sketch_text.stroke-39")])]})]});
            var Q31;
            Q31=makeQuery(id+"F2.opFillet","BLEND_EDGE",EDGE,{"blendedFrom":[makeQuery(id+"F1.opExtrude","CAP_EDGE",EDGE,{"disambiguationData":[OSD([sQuery(id+"F0.wireOp",EDGE,"E1.top")])],"isStart":true}),makeQuery(id+"F1.opExtrude","SWEPT_FACE",FACE,{"disambiguationData":[OSD([sQuery(id+"F0.wireOp",EDGE,"E0.sketch_text.stroke-21")])]})],"blendedInto":[makeQuery(id+"F1.opExtrude","SWEPT_FACE",FACE,{"disambiguationData":[OSD([sQuery(id+"F0.wireOp",EDGE,"E0.sketch_text.stroke-21")])]})]});
            var Q32;
            {var subQ0=sQuery(id+"F0.wireOp",EDGE,"E1.top");Q32=makeQuery(id+"F6.opFillet","BLEND_EDGE",EDGE,{"blendedFrom":[makeQuery(id+"F1.opExtrude","SWEPT_EDGE",EDGE,{"disambiguationData":[OSD([sQuery(id+"F0.wireOp",EDGE,"E0.sketch_text.stroke-21"),sQuery(id+"F0.wireOp",EDGE,"E0.sketch_text.stroke-22")])]}),makeQuery(id+"F2.opFillet","BLEND_FACE",FACE,{"disambiguationData":[OSD([subQ0]),TDD([makeQuery(id+"F1.opExtrude","CAP_EDGE",EDGE,{"disambiguationData":[OSD([subQ0])],"isStart":true})])]})],"blendedInto":[makeQuery(id+"F2.opFillet","BLEND_FACE",FACE,{"disambiguationData":[OSD([subQ0]),TDD([makeQuery(id+"F1.opExtrude","CAP_EDGE",EDGE,{"disambiguationData":[OSD([subQ0])],"isStart":true})])]})]});}
            var Q33;
            {var subQ0=sQuery(id+"F0.wireOp",EDGE,"E0.sketch_text.stroke-15");Q33=makeQuery(id+"F6.opFillet","BLEND_EDGE",EDGE,{"blendedFrom":[makeQuery(id+"F1.opExtrude","CAP_EDGE",EDGE,{"disambiguationData":[OSD([subQ0])],"isStart":true}),makeQuery(id+"F1.opExtrude","SWEPT_FACE",FACE,{"disambiguationData":[OSD([subQ0])]})],"blendedInto":[makeQuery(id+"F1.opExtrude","SWEPT_FACE",FACE,{"disambiguationData":[OSD([subQ0])]})]});}
            var Q34;
            {var subQ0=sQuery(id+"F0.wireOp",EDGE,"E0.sketch_text.stroke-15");Q34=makeQuery(id+"F6.opFillet","BLEND_EDGE",EDGE,{"blendedFrom":[makeQuery(id+"F1.opExtrude","CAP_EDGE",EDGE,{"disambiguationData":[OSD([subQ0])],"isStart":true}),makeQuery(id+"F1.opExtrude","SWEPT_EDGE",EDGE,{"disambiguationData":[OSD([subQ0,sQuery(id+"F0.wireOp",EDGE,"E0.sketch_text.stroke-22")])]})],"blendedInto":[]});}
            var Q35;
            Q35=makeQuery(id+"F1.opExtrude","CAP_EDGE",EDGE,{"disambiguationData":[OSD([sQuery(id+"F0.wireOp",EDGE,"E0.sketch_text.stroke-22")])],"isStart":true});
            fillet(context, id + "F8", {"entities" : qUnion([Q0, Q1, Q2, Q3, Q4, Q5, Q6, Q7, Q8, Q9, Q10, Q11, Q12, Q13, Q14, Q15, Q16, Q17, Q18, Q19, Q20, Q21, Q22, Q23, Q24, Q25, Q26, Q27, Q28, Q29, Q30, Q31, Q32, Q33, Q34, Q35]), "radius" : 0.5 * mm, "tangentPropagation" : true, "allowEdgeOverflow" : false});
        }
    });
